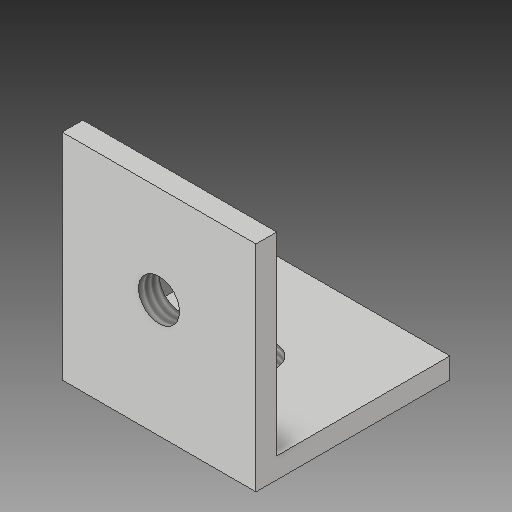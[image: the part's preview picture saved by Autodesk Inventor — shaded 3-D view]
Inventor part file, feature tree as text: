
AUTODESK INVENTOR PART (.ipt)
format: ipt  version: 2019 (Build 230136000, 136)  size: 117,248 bytes
history: native  units: mm
features: sketch x4, extrude x2, hole x2
ambient origin geometry x8: Origin, YZ Plane, XZ Plane, XY Plane, X Axis, Y Axis, Z Axis, Center Point
bodies: Solid1 (feature_tree)
feature tree (8):
  extrude  "Extrusion1"  Depth=28.0mm
  hole  "Hole1"  [1 undecoded]
  extrude  "Extrusion2"  Depth=3.0mm
  hole  "Hole2"  [1 undecoded]
  sketch  "Sketch1"  dims[d0=28.0mm d1=28.0mm]
  sketch  "Sketch2"  dims[d2=3.0mm d3=0.0mm d4=14.0mm]
  sketch  "Sketch3"  dims[d5=14.0mm]
  sketch  "Sketch4"  dims[d6=5.917mm d7=14.0mm d8=4.0mm d9=2.0mm d10=90.0deg d11=19.1mm d12=20.594885mm d13=3.0mm d14=28.0mm d15=0.0mm d16=14.0mm d17=14.0mm d18=5.917mm d19=14.0mm d20=4.0mm d21=2.0mm d22=90.0deg d23=19.1mm d24=20.594885mm]
note: 2 required parameter values undecoded (feature->parameter linkage not recoverable at this tier; creation-order binding heuristic only, values carry confidence <= 0.55)
